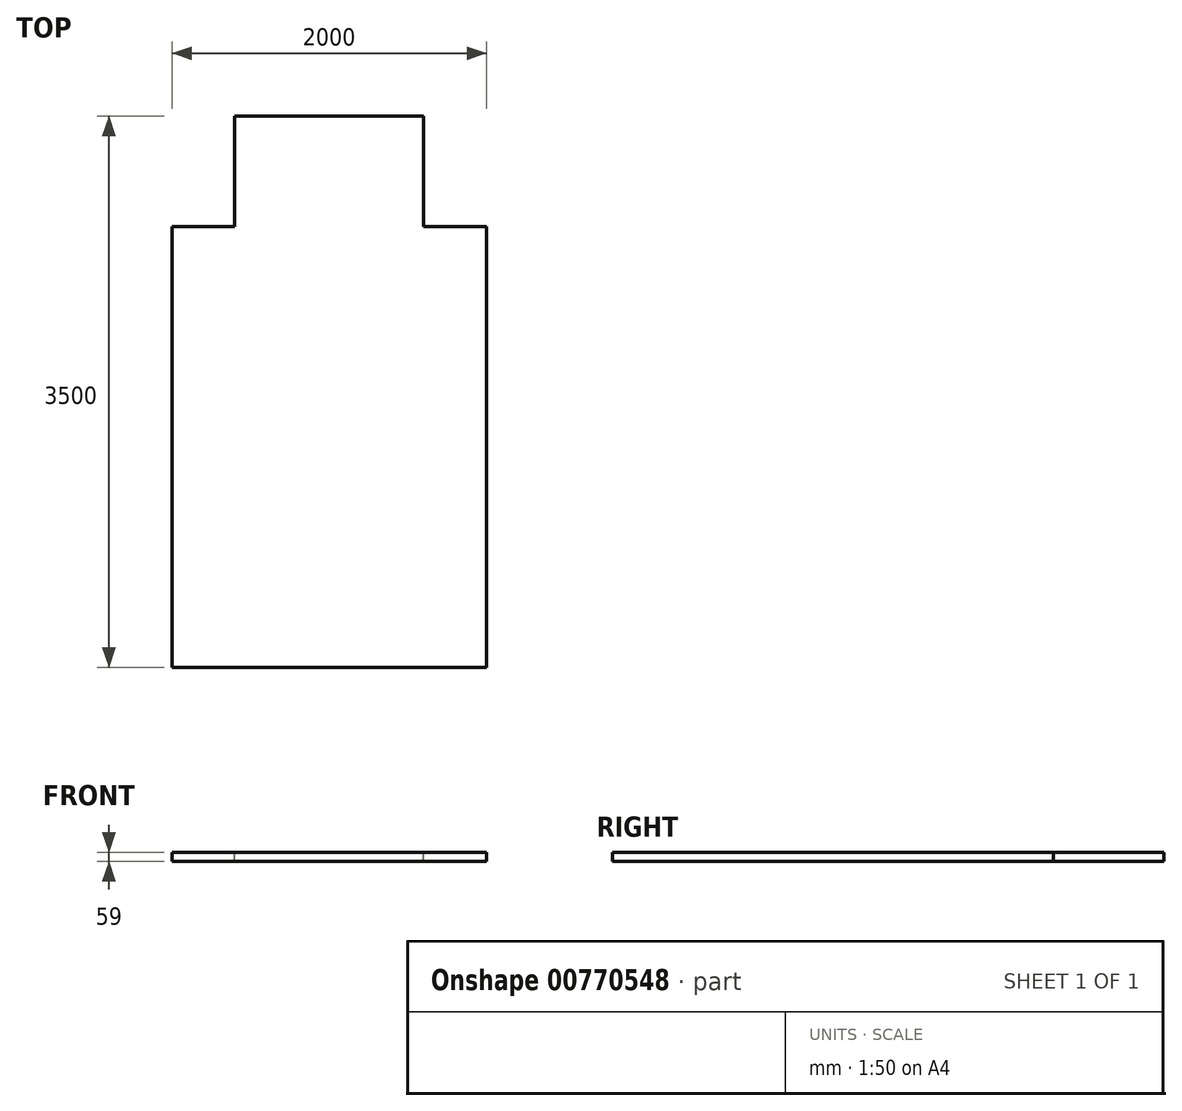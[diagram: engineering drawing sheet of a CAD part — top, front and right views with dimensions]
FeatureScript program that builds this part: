
annotation { "Feature Type Name" : "Feature", "Feature Type Description" : "" }
export const myFeature = defineFeature(function(context is Context, id is Id, definition is map)
    precondition{}
    {
        {
            var Q0;
            Q0=qCreatedBy(makeId("Top.planeOp"),FACE);
            var sketch = newSketch(context, id + "F0", { "sketchPlane" : qUnion([Q0])});
            skLineSegment(sketch, "E0.bottom", {"start": v(-1000, 1750) * mm, "end": v(1000, 1750) * mm});
            skLineSegment(sketch, "E0.top", {"start": v(-1000, -1750) * mm, "end": v(1000, -1750) * mm});
            skLineSegment(sketch, "E0.left", {"start": v(-1000, 1750) * mm, "end": v(-1000, -1750) * mm});
            skLineSegment(sketch, "E0.right", {"start": v(1000, 1750) * mm, "end": v(1000, -1750) * mm});
            skPoint(sketch, "E0.middle", {"position": v(0, 0) * mm});
            skSolve(sketch);
        }
        {
            var Q0;
            Q0 = qSketchRegion(id + "F0", true);
            extrude(context, id + "F1", {"entities" : qUnion([Q0]), "depth" : 59 * mm, "offsetDistance" : 25 * mm});
        }
        {
            var Q0;
            Q0=makeQuery(id+"F1.opExtrude","CAP_FACE",FACE,{"disambiguationData":[OSD([sQuery(id+"F0.wireOp",EDGE,"E0.bottom"),sQuery(id+"F0.wireOp",EDGE,"E0.top"),sQuery(id+"F0.wireOp",EDGE,"E0.left"),sQuery(id+"F0.wireOp",EDGE,"E0.right")])],"isStart":false});
            var sketch = newSketch(context, id + "F2", { "sketchPlane" : qUnion([Q0])});
            skLineSegment(sketch, "E1", {"start": v(-600, 1750) * mm, "end": v(-600, 1050) * mm});
            skLineSegment(sketch, "E2", {"start": v(-600, 1050) * mm, "end": v(-1000, 1050) * mm});
            skLineSegment(sketch, "E3", {"start": v(0, 1750) * mm, "end": v(0, -1750) * mm});
            skLineSegment(sketch, "E4.MirrorCS", {"start": v(600, 1750) * mm, "end": v(600, 1050) * mm});
            skLineSegment(sketch, "E5.MirrorCS", {"start": v(600, 1050) * mm, "end": v(1000, 1050) * mm});
            skSolve(sketch);
        }
        {
            var Q0;
            {var subQ0=sQuery(id+"F2.wireOp",EDGE,"E1");Q0=makeQuery(id+"F2.imprint","IMPRINT",FACE,{"disambiguationData":[TD([[makeQuery(id+"F2.imprint","IMPRINT",EDGE,{"derivedFrom":subQ0}),-1.0]])]});}
            var Q1;
            {var subQ0=sQuery(id+"F2.wireOp",EDGE,"E4.MirrorCS");Q1=makeQuery(id+"F2.imprint","IMPRINT",FACE,{"disambiguationData":[TD([[makeQuery(id+"F2.imprint","IMPRINT",EDGE,{"derivedFrom":subQ0}),1.0]])]});}
            extrude(context, id + "F3", {"entities" : qUnion([Q0, Q1]), "operationType" : NewBodyOperationType.REMOVE, "endBound" : BoundingType.THROUGH_ALL, "oppositeDirection" : true, "depth" : 25 * mm, "offsetDistance" : 25 * mm});
        }
    });
